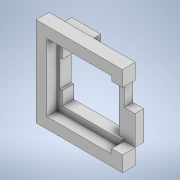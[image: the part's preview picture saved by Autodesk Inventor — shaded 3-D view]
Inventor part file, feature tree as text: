
AUTODESK INVENTOR PART (.ipt)
format: ipt  version: 2020 (Build 240168000, 168)  size: 214,016 bytes
history: native  units: in
note: dims shown in document units (in); Inventor stores cm internally (conversion verified against a paired STEP export)
features: extrude x3, sketch x3, projected_geometry x2
ambient origin geometry x8: Origin, YZ Plane, XZ Plane, XY Plane, X Axis, Y Axis, Z Axis, Center Point
bodies: Solid1 (feature_tree)
feature tree (8):
  extrude  "Extrusion1"  Depth=0.0438in
  extrude  "Extrusion2"  Depth=0.1575in
  extrude  "Extrusion3"  Depth=0.4685in
  sketch  "Sketch1"  dims[d0=0.9449in d1=0.0438in]
  sketch  "Sketch2"  dims[d2=0.1575in d3=0.4331in]
  sketch  "Sketch3"  dims[d4=0.468in d5=0.4685in d6=0.1575in d7=0.4331in d8=0.0433in d9=0.0039in d10=0.1219in d11=1.1012in d12=1.1028in d13=0.126in d14=0.0in d15=0.7874in d16=0.0374in d17=0.3937in d18=0.987in d19=0.9449in d20=0.1575in d21=0.0683in d22=0.0683in d23=0.187in d24=0.0in d25=0.0394in d26=0.0in]
  projected_geometry  "Projected Loop1"
  projected_geometry  "Projected Loop2"
